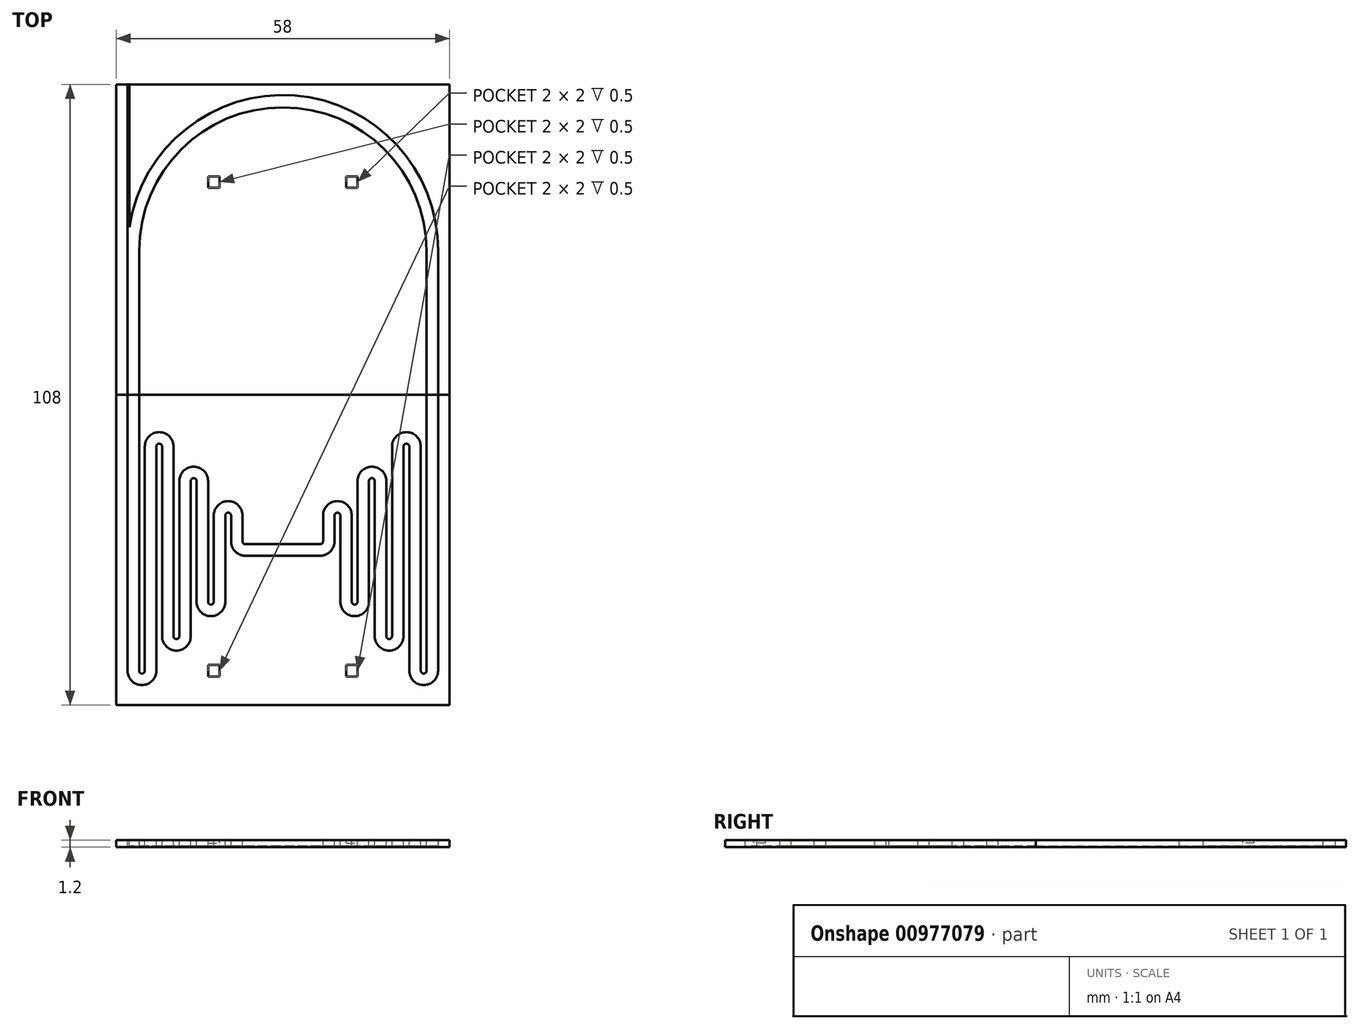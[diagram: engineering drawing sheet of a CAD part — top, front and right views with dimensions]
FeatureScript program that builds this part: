
annotation { "Feature Type Name" : "Feature", "Feature Type Description" : "" }
export const myFeature = defineFeature(function(context is Context, id is Id, definition is map)
    precondition{}
    {
        {
            var Q0;
            Q0=qCreatedBy(makeId("Top.planeOp"),FACE);
            var sketch = newSketch(context, id + "F0", { "sketchPlane" : qUnion([Q0])});
            skLineSegment(sketch, "E0.bottom", {"start": v(29, 27) * mm, "end": v(-29, 27) * mm});
            skLineSegment(sketch, "E0.top", {"start": v(29, -27) * mm, "end": v(-29, -27) * mm});
            skLineSegment(sketch, "E0.left", {"start": v(29, 27) * mm, "end": v(29, -27) * mm});
            skLineSegment(sketch, "E0.right", {"start": v(-29, 27) * mm, "end": v(-29, -27) * mm});
            skPoint(sketch, "E0.middle", {"position": v(0, 0) * mm});
            skSolve(sketch);
        }
        {
            var Q0;
            Q0=makeQuery(id+"F0.imprint","IMPRINT",FACE,{"disambiguationData":[TD([[makeQuery(id+"F0.imprint","IMPRINT",EDGE,{"derivedFrom":sQuery(id+"F0.wireOp",EDGE,"E0.bottom")}),1.0]])]});
            extrude(context, id + "F1", {"entities" : qUnion([Q0]), "depth" : 1.2 * mm, "offsetDistance" : 25 * mm});
        }
        {
            var Q0;
            Q0=makeQuery(id+"F1.opExtrude","CAP_FACE",FACE,{"disambiguationData":[OSD([sQuery(id+"F0.wireOp",EDGE,"E0.bottom"),sQuery(id+"F0.wireOp",EDGE,"E0.top"),sQuery(id+"F0.wireOp",EDGE,"E0.left"),sQuery(id+"F0.wireOp",EDGE,"E0.right")])],"isStart":false});
            var sketch = newSketch(context, id + "F2", { "sketchPlane" : qUnion([Q0])});
            skPoint(sketch, "E1.middle", {"position": v(-28, 0) * mm});
            skLineSegment(sketch, "E2.left", {"start": v(-27, 25) * mm, "end": v(-27, -21) * mm});
            skLineSegment(sketch, "E2.right", {"start": v(-25, 23.27) * mm, "end": v(-25, -21) * mm});
            skLineSegment(sketch, "E3.left", {"start": v(-25, 18) * mm, "end": v(-25, -21) * mm});
            skLineSegment(sketch, "E3.right", {"start": v(-24, 18) * mm, "end": v(-24, -21) * mm});
            skLineSegment(sketch, "E4.right", {"start": v(-22, 18) * mm, "end": v(-22, -21) * mm});
            skLineSegment(sketch, "E5.left", {"start": v(-21, 18) * mm, "end": v(-21, -15) * mm});
            skLineSegment(sketch, "E5.right", {"start": v(-19, 18) * mm, "end": v(-19, -15) * mm});
            skLineSegment(sketch, "E6.left", {"start": v(-18, 12) * mm, "end": v(-18, -15) * mm});
            skLineSegment(sketch, "E6.right", {"start": v(-16, 12) * mm, "end": v(-16, -15) * mm});
            skLineSegment(sketch, "E7.left", {"start": v(-15, 12) * mm, "end": v(-15, -9) * mm});
            skLineSegment(sketch, "E7.right", {"start": v(-13, 12) * mm, "end": v(-13, -9) * mm});
            skLineSegment(sketch, "E8.left", {"start": v(-12, 6) * mm, "end": v(-12, -9) * mm});
            skLineSegment(sketch, "E8.right", {"start": v(-10, 6) * mm, "end": v(-10, -9) * mm});
            skPoint(sketch, "E9.firstSnap0", {"position": v(-13, 1.5) * mm});
            skLineSegment(sketch, "E10.left", {"start": v(-9, 6) * mm, "end": v(-9, 1.5) * mm});
            skLineSegment(sketch, "E10.right", {"start": v(-7, 6) * mm, "end": v(-7, 1.5) * mm});
            skLineSegment(sketch, "E11.bottom", {"start": v(6.5, 1) * mm, "end": v(-6.5, 1) * mm});
            skLineSegment(sketch, "E11.top", {"start": v(6.5, -1) * mm, "end": v(-6.5, -1) * mm});
            skPoint(sketch, "E11.middle", {"position": v(0, 0) * mm});
            skArc(sketch, "E12", {"start": v(-9, 6) * mm, "mid": v(-9.5, 6.5) * mm, "end": v(-10, 6) * mm});
            skArc(sketch, "E13", {"start": v(-7, 6) * mm, "mid": v(-9.5, 8.5) * mm, "end": v(-12, 6) * mm});
            skArc(sketch, "E14", {"start": v(-13, -9) * mm, "mid": v(-12.5, -9.5) * mm, "end": v(-12, -9) * mm});
            skArc(sketch, "E15", {"start": v(-15, -9) * mm, "mid": v(-12.5, -11.5) * mm, "end": v(-10, -9) * mm});
            skArc(sketch, "E16", {"start": v(-15, 12) * mm, "mid": v(-15.5, 12.5) * mm, "end": v(-16, 12) * mm});
            skArc(sketch, "E17", {"start": v(-13, 12) * mm, "mid": v(-15.5, 14.5) * mm, "end": v(-18, 12) * mm});
            skArc(sketch, "E18", {"start": v(-19, -15) * mm, "mid": v(-18.5, -15.5) * mm, "end": v(-18, -15) * mm});
            skArc(sketch, "E19", {"start": v(-21, -15) * mm, "mid": v(-18.5, -17.5) * mm, "end": v(-16, -15) * mm});
            skArc(sketch, "E20", {"start": v(-21, 18) * mm, "mid": v(-21.5, 18.5) * mm, "end": v(-22, 18) * mm});
            skArc(sketch, "E21", {"start": v(-19, 18) * mm, "mid": v(-21.5, 20.5) * mm, "end": v(-24, 18) * mm});
            skArc(sketch, "E22", {"start": v(-25, -21) * mm, "mid": v(-24.5, -21.5) * mm, "end": v(-24, -21) * mm});
            skArc(sketch, "E23", {"start": v(-27, -21) * mm, "mid": v(-24.5, -23.5) * mm, "end": v(-22, -21) * mm});
            skArc(sketch, "E24", {"start": v(-7, 1.5) * mm, "mid": v(-6.86, 1.14) * mm, "end": v(-6.5, 1) * mm});
            skArc(sketch, "E25", {"start": v(-9, 1.5) * mm, "mid": v(-8.27, -0.27) * mm, "end": v(-6.5, -1) * mm});
            skLineSegment(sketch, "E26.left", {"start": v(25, 25) * mm, "end": v(25, -21) * mm});
            skLineSegment(sketch, "E26.right", {"start": v(27, 23.27) * mm, "end": v(27, -21) * mm});
            skLineSegment(sketch, "E27.right", {"start": v(25, 23.27) * mm, "end": v(25, -22.73) * mm});
            skLineSegment(sketch, "E28.left", {"start": v(22, 18) * mm, "end": v(22, -21) * mm});
            skLineSegment(sketch, "E28.right", {"start": v(24, 18) * mm, "end": v(24, -21) * mm});
            skLineSegment(sketch, "E29.left", {"start": v(19, 18) * mm, "end": v(19, -15) * mm});
            skLineSegment(sketch, "E29.right", {"start": v(21, 18) * mm, "end": v(21, -15) * mm});
            skLineSegment(sketch, "E30.left", {"start": v(16, 12) * mm, "end": v(16, -15) * mm});
            skLineSegment(sketch, "E30.right", {"start": v(18, 12) * mm, "end": v(18, -15) * mm});
            skLineSegment(sketch, "E31.right", {"start": v(16, 12) * mm, "end": v(16, -16.73) * mm});
            skLineSegment(sketch, "E32.left", {"start": v(13, 12) * mm, "end": v(13, -9) * mm});
            skLineSegment(sketch, "E32.right", {"start": v(15, 12) * mm, "end": v(15, -9) * mm});
            skLineSegment(sketch, "E33.left", {"start": v(10, 6) * mm, "end": v(10, -9) * mm});
            skLineSegment(sketch, "E33.right", {"start": v(12, 6) * mm, "end": v(12, -9) * mm});
            skLineSegment(sketch, "E34.left", {"start": v(7, 6) * mm, "end": v(7, 1.5) * mm});
            skLineSegment(sketch, "E34.right", {"start": v(9, 6) * mm, "end": v(9, 1.5) * mm});
            skArc(sketch, "E35", {"start": v(6.5, 1) * mm, "mid": v(6.85, 1.14) * mm, "end": v(7, 1.5) * mm});
            skArc(sketch, "E36", {"start": v(6.5, -1) * mm, "mid": v(8.26, -0.27) * mm, "end": v(9, 1.5) * mm});
            skArc(sketch, "E37", {"start": v(22, -21) * mm, "mid": v(24.5, -23.5) * mm, "end": v(27, -21) * mm});
            skArc(sketch, "E38", {"start": v(24, -21) * mm, "mid": v(24.5, -21.5) * mm, "end": v(25, -21) * mm});
            skArc(sketch, "E39", {"start": v(18, -15) * mm, "mid": v(18.5, -15.5) * mm, "end": v(19, -15) * mm});
            skArc(sketch, "E40", {"start": v(16, -15) * mm, "mid": v(18.5, -17.5) * mm, "end": v(21, -15) * mm});
            skArc(sketch, "E41", {"start": v(12, -9) * mm, "mid": v(12.5, -9.5) * mm, "end": v(13, -9) * mm});
            skArc(sketch, "E42", {"start": v(10, -9) * mm, "mid": v(12.5, -11.5) * mm, "end": v(15, -9) * mm});
            skArc(sketch, "E43", {"start": v(22, 18) * mm, "mid": v(21.5, 18.5) * mm, "end": v(21, 18) * mm});
            skArc(sketch, "E44", {"start": v(24, 18) * mm, "mid": v(21.5, 20.5) * mm, "end": v(19, 18) * mm});
            skArc(sketch, "E45", {"start": v(16, 12) * mm, "mid": v(15.5, 12.5) * mm, "end": v(15, 12) * mm});
            skArc(sketch, "E46", {"start": v(18, 12) * mm, "mid": v(15.5, 14.5) * mm, "end": v(13, 12) * mm});
            skArc(sketch, "E47", {"start": v(10, 6) * mm, "mid": v(9.5, 6.5) * mm, "end": v(9, 6) * mm});
            skArc(sketch, "E48", {"start": v(12, 6) * mm, "mid": v(9.5, 8.5) * mm, "end": v(7, 6) * mm});
            skLineSegment(sketch, "E49.top", {"start": v(-27, 27) * mm, "end": v(-25, 27) * mm});
            skLineSegment(sketch, "E49.left", {"start": v(-27, 25) * mm, "end": v(-27, 27) * mm});
            skLineSegment(sketch, "E49.right", {"start": v(-25, 25) * mm, "end": v(-25, 27) * mm});
            skLineSegment(sketch, "E50.top", {"start": v(25, 27) * mm, "end": v(27, 27) * mm});
            skLineSegment(sketch, "E50.left", {"start": v(25, 23.27) * mm, "end": v(25, 27) * mm});
            skLineSegment(sketch, "E50.right", {"start": v(27, 25) * mm, "end": v(27, 27) * mm});
            skLineSegment(sketch, "E51", {"start": v(27, 25) * mm, "end": v(27, 23.27) * mm});
            skLineSegment(sketch, "E52", {"start": v(-25, 25) * mm, "end": v(-25, 23.27) * mm});
            skSolve(sketch);
        }
        {
            var Q0;
            Q0=makeQuery(id+"F2.imprint","IMPRINT",FACE,{"disambiguationData":[TD([[makeQuery(id+"F2.imprint","IMPRINT",EDGE,{"derivedFrom":sQuery(id+"F2.wireOp",EDGE,"E2.left")}),1.0]])]});
            extrude(context, id + "F3", {"entities" : qUnion([Q0]), "operationType" : NewBodyOperationType.REMOVE, "oppositeDirection" : true, "depth" : 1 * mm, "offsetDistance" : 25 * mm});
        }
        {
            var Q0;
            Q0=qCreatedBy(makeId("Top.planeOp"),FACE);
            var sketch = newSketch(context, id + "F4", { "sketchPlane" : qUnion([Q0])});
            skLineSegment(sketch, "E53.bottom", {"start": v(-29, 27) * mm, "end": v(29, 27) * mm});
            skLineSegment(sketch, "E53.top", {"start": v(-29, 81) * mm, "end": v(29, 81) * mm});
            skLineSegment(sketch, "E53.left", {"start": v(-29, 27) * mm, "end": v(-29, 81) * mm});
            skLineSegment(sketch, "E53.right", {"start": v(29, 27) * mm, "end": v(29, 81) * mm});
            skSolve(sketch);
        }
        {
            var Q0;
            Q0=makeQuery(id+"F4.imprint","IMPRINT",FACE,{"disambiguationData":[TD([[makeQuery(id+"F4.imprint","IMPRINT",EDGE,{"derivedFrom":sQuery(id+"F4.wireOp",EDGE,"E53.bottom")}),1.0]])]});
            extrude(context, id + "F5", {"entities" : qUnion([Q0]), "depth" : 1.2 * mm, "offsetDistance" : 25 * mm});
        }
        {
            var Q0;
            Q0=makeQuery(id+"F5.opExtrude","CAP_FACE",FACE,{"disambiguationData":[OSD([sQuery(id+"F4.wireOp",EDGE,"E53.bottom"),sQuery(id+"F4.wireOp",EDGE,"E53.top"),sQuery(id+"F4.wireOp",EDGE,"E53.left"),sQuery(id+"F4.wireOp",EDGE,"E53.right")])],"isStart":false});
            var sketch = newSketch(context, id + "F6", { "sketchPlane" : qUnion([Q0])});
            skLineSegment(sketch, "E54.bottom", {"start": v(-27, 27) * mm, "end": v(-25, 27) * mm});
            skLineSegment(sketch, "E54.top", {"start": v(-27, 52) * mm, "end": v(-25, 52) * mm});
            skLineSegment(sketch, "E54.left", {"start": v(-27, 27) * mm, "end": v(-27, 52) * mm});
            skLineSegment(sketch, "E54.right", {"start": v(-25, 27) * mm, "end": v(-25, 52) * mm});
            skLineSegment(sketch, "E55.bottom", {"start": v(27, 27) * mm, "end": v(25, 27) * mm});
            skLineSegment(sketch, "E55.top", {"start": v(27, 52) * mm, "end": v(25, 52) * mm});
            skLineSegment(sketch, "E55.left", {"start": v(27, 27) * mm, "end": v(27, 52) * mm});
            skLineSegment(sketch, "E55.right", {"start": v(25, 27) * mm, "end": v(25, 52) * mm});
            skArc(sketch, "E56", {"start": v(25, 52) * mm, "mid": v(0, 77) * mm, "end": v(-25, 52) * mm});
            skArc(sketch, "E57", {"start": v(27, 52) * mm, "mid": v(0, 79.13) * mm, "end": v(-27, 52) * mm});
            skPoint(sketch, "E57.startSnap0", {"position": v(27, 39.5) * mm});
            skLineSegment(sketch, "E58.bottom", {"start": v(-27, 52) * mm, "end": v(-26.7, 52) * mm});
            skLineSegment(sketch, "E58.top", {"start": v(-27, 81) * mm, "end": v(-26.7, 81) * mm});
            skLineSegment(sketch, "E58.left", {"start": v(-27, 52) * mm, "end": v(-27, 81) * mm});
            skLineSegment(sketch, "E58.right", {"start": v(-26.7, 52) * mm, "end": v(-26.7, 81) * mm});
            skSolve(sketch);
        }
        {
            var Q0;
            Q0=qSketchRegion(id+"F6",true);
            extrude(context, id + "F7", {"entities" : qUnion([Q0]), "operationType" : NewBodyOperationType.REMOVE, "oppositeDirection" : true, "depth" : 1 * mm, "offsetDistance" : 25 * mm});
        }
        {
            var Q0;
            Q0=makeQuery(id+"F2.imprint","IMPRINT",FACE,{"disambiguationData":[TD([[makeQuery(id+"F2.imprint","IMPRINT",EDGE,{"derivedFrom":sQuery(id+"F2.wireOp",EDGE,"E2.left")}),-1.0]])]});
            var sketch = newSketch(context, id + "F8", { "sketchPlane" : qUnion([Q0])});
            skLineSegment(sketch, "E59.bottom", {"start": v(-13, -22) * mm, "end": v(-11, -22) * mm});
            skLineSegment(sketch, "E59.top", {"start": v(-13, -20) * mm, "end": v(-11, -20) * mm});
            skLineSegment(sketch, "E59.left", {"start": v(-13, -22) * mm, "end": v(-13, -20) * mm});
            skLineSegment(sketch, "E59.right", {"start": v(-11, -22) * mm, "end": v(-11, -20) * mm});
            skPoint(sketch, "E60.oppositeSnap0", {"position": v(-12, -22) * mm});
            skLineSegment(sketch, "E60.bottom", {"start": v(11, -20) * mm, "end": v(13, -20) * mm});
            skLineSegment(sketch, "E60.top", {"start": v(11, -22) * mm, "end": v(13, -22) * mm});
            skLineSegment(sketch, "E60.left", {"start": v(11, -20) * mm, "end": v(11, -22) * mm});
            skLineSegment(sketch, "E60.right", {"start": v(13, -20) * mm, "end": v(13, -22) * mm});
            skSolve(sketch);
        }
        {
            var Q0;
            Q0 = qSketchRegion(id + "F8", true);
            extrude(context, id + "F9", {"entities" : qUnion([Q0]), "operationType" : NewBodyOperationType.REMOVE, "oppositeDirection" : true, "depth" : 0.5 * mm, "offsetDistance" : 25 * mm});
        }
        {
            var Q0;
            {var subQ2=sQuery(id+"F6.wireOp",EDGE,"E55.right");Q0=makeQuery(id+"F6.imprint","IMPRINT",FACE,{"disambiguationData":[TD([[makeQuery(id+"F6.imprint","IMPRINT",EDGE,{"derivedFrom":subQ2}),1.0]])]});}
            var sketch = newSketch(context, id + "F10", { "sketchPlane" : qUnion([Q0])});
            skLineSegment(sketch, "E61.bottom", {"start": v(-13, 65) * mm, "end": v(-11, 65) * mm});
            skLineSegment(sketch, "E61.top", {"start": v(-13, 63) * mm, "end": v(-11, 63) * mm});
            skLineSegment(sketch, "E61.left", {"start": v(-13, 65) * mm, "end": v(-13, 63) * mm});
            skLineSegment(sketch, "E61.right", {"start": v(-11, 65) * mm, "end": v(-11, 63) * mm});
            skLineSegment(sketch, "E62.bottom", {"start": v(11, 65) * mm, "end": v(13, 65) * mm});
            skLineSegment(sketch, "E62.top", {"start": v(11, 63) * mm, "end": v(13, 63) * mm});
            skLineSegment(sketch, "E62.left", {"start": v(11, 65) * mm, "end": v(11, 63) * mm});
            skLineSegment(sketch, "E62.right", {"start": v(13, 65) * mm, "end": v(13, 63) * mm});
            skSolve(sketch);
        }
        {
            var Q0;
            Q0 = qSketchRegion(id + "F10", true);
            extrude(context, id + "F11", {"entities" : qUnion([Q0]), "operationType" : NewBodyOperationType.REMOVE, "oppositeDirection" : true, "depth" : 0.5 * mm, "offsetDistance" : 25 * mm});
        }
    });
